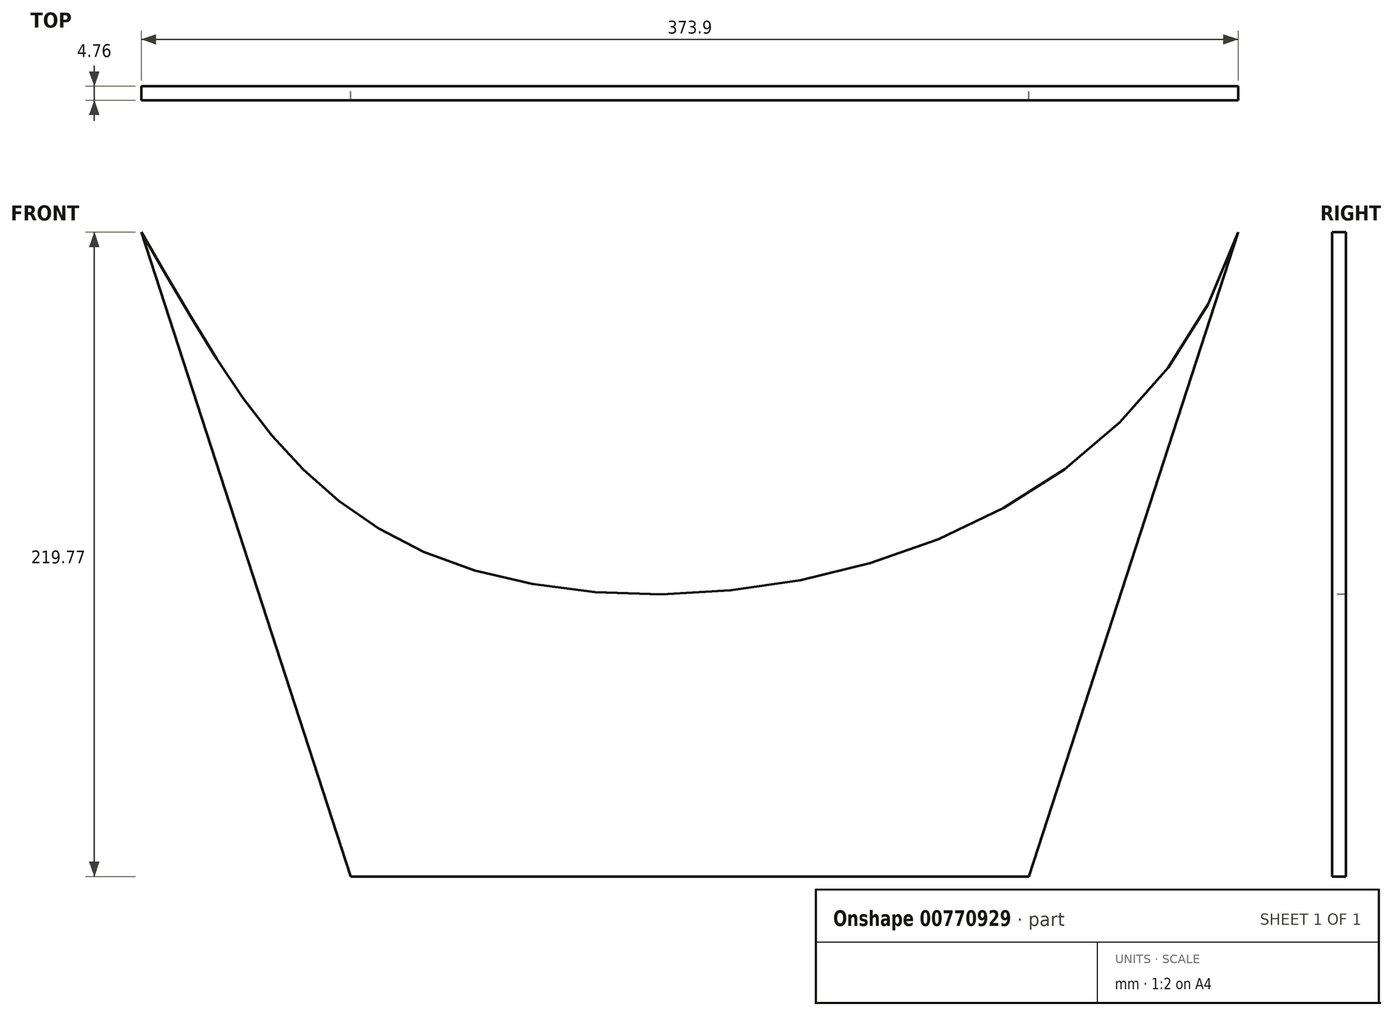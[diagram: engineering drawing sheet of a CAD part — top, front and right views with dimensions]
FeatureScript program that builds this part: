
annotation { "Feature Type Name" : "Feature", "Feature Type Description" : "" }
export const myFeature = defineFeature(function(context is Context, id is Id, definition is map)
    precondition{}
    {
        {
            var Q0;
            Q0=qCreatedBy(makeId("Front.planeOp"),FACE);
            var sketch = newSketch(context, id + "F0", { "sketchPlane" : qUnion([Q0])});
            skCircle(sketch, "E0.cCircle", {"center": v(0, 0) * mm, "radius": 159.03 * mm, "construction": true});
            skLineSegment(sketch, "E0.0", {"start": v(115.54, -159.03) * mm, "end": v(-115.54, -159.03) * mm});
            skLineSegment(sketch, "E0.1", {"start": v(-115.54, -159.03) * mm, "end": v(-186.95, 60.74) * mm});
            skLineSegment(sketch, "E0.4", {"start": v(186.95, 60.74) * mm, "end": v(115.54, -159.03) * mm});
            skPoint(sketch, "E0.0.midPoint", {"position": v(0, -159.03) * mm});
            skFitSpline(sketch, "E1", {"points": [v(-186.95, 60.74) * mm, v(-76.75, -53.61) * mm, v(186.95, 60.74) * mm], "startDerivative": vector(199.93, -339.2) * mm, "endDerivative": vector(195.27, 600.97) * mm});
            skSolve(sketch);
        }
        {
            var Q0;
            Q0=makeQuery(id+"F0.imprint","IMPRINT",FACE,{"disambiguationData":[TD([[makeQuery(id+"F0.imprint","IMPRINT",EDGE,{"derivedFrom":sQuery(id+"F0.wireOp",EDGE,"E0.0")}),-1.0]])]});
            extrude(context, id + "F1", {"entities" : qUnion([Q0]), "endBound" : BoundingType.SYMMETRIC, "depth" : 4.76 * mm, "offsetDistance" : 25.4 * mm});
        }
    });
